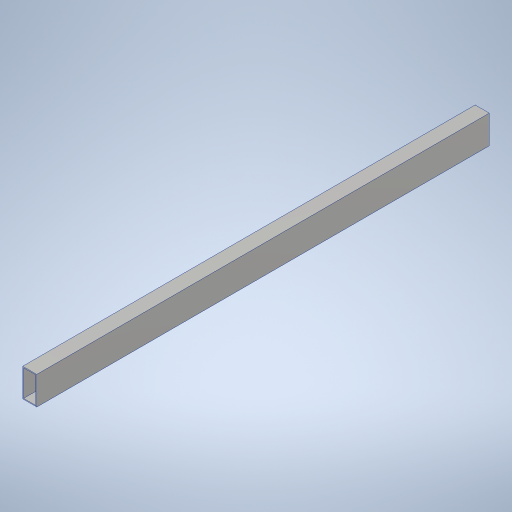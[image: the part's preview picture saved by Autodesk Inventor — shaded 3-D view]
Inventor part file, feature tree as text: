
AUTODESK INVENTOR PART (.ipt)
format: ipt  version: 2023.4 (Build 274418000, 418)  size: 241,664 bytes
history: native  units: in
note: dims shown in document units (in); Inventor stores cm internally (conversion verified against a paired STEP export)
features: extrude x1
ambient origin geometry x8: Origin, YZ Plane, XZ Plane, XY Plane, X Axis, Y Axis, Z Axis, Center Point
bodies: Solid1 (feature_tree)
feature tree (1):
  extrude  "Extrusion1"  TaperAngle=0.0deg  [1 undecoded]
note: 1 required parameter value undecoded (feature->parameter linkage not recoverable at this tier; creation-order binding heuristic only, values carry confidence <= 0.55)
